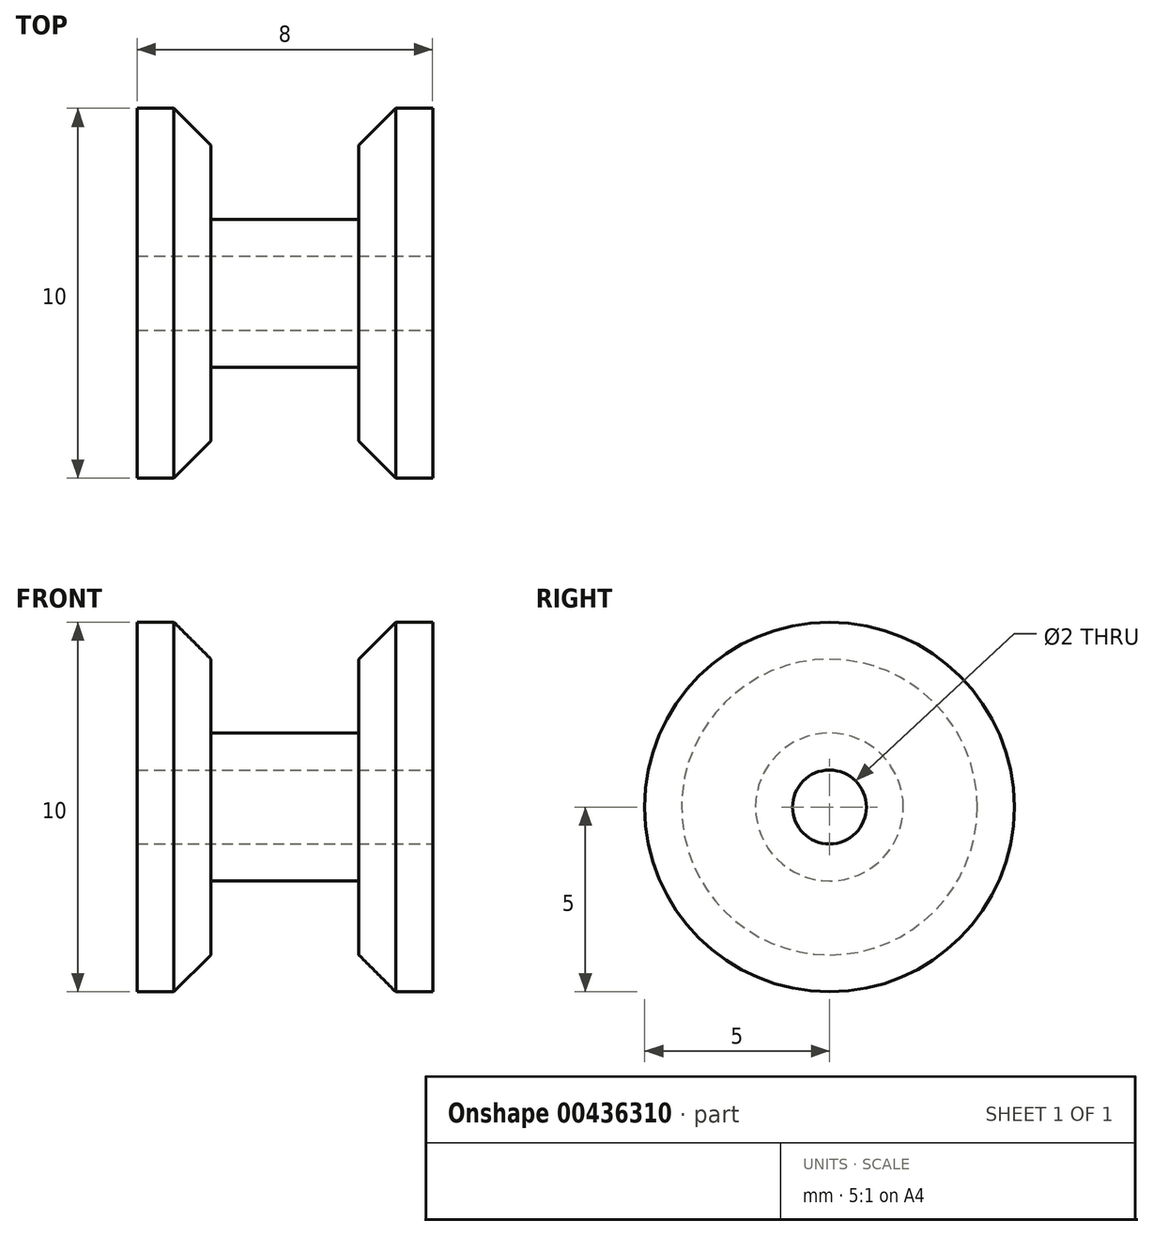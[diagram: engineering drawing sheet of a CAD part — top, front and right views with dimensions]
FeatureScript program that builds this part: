
annotation { "Feature Type Name" : "Feature", "Feature Type Description" : "" }
export const myFeature = defineFeature(function(context is Context, id is Id, definition is map)
    precondition{}
    {
        {
            var Q0;
            Q0=qCreatedBy(makeId("Top.planeOp"),FACE);
            var sketch = newSketch(context, id + "F0", { "sketchPlane" : qUnion([Q0])});
            skLineSegment(sketch, "E0", {"start": v(-2.83, 0) * mm, "end": v(-2.83, 5) * mm});
            skLineSegment(sketch, "E1", {"start": v(-2.83, 5) * mm, "end": v(-0.83, 5) * mm});
            skLineSegment(sketch, "E2", {"start": v(-0.83, 5) * mm, "end": v(-0.83, 2) * mm});
            skLineSegment(sketch, "E3", {"start": v(-0.83, 2) * mm, "end": v(3.17, 2) * mm});
            skLineSegment(sketch, "E4", {"start": v(3.17, 2) * mm, "end": v(3.17, 5) * mm});
            skLineSegment(sketch, "E5", {"start": v(3.17, 5) * mm, "end": v(5.17, 5) * mm});
            skLineSegment(sketch, "E6", {"start": v(5.17, 5) * mm, "end": v(5.17, 0) * mm});
            skLineSegment(sketch, "E7", {"start": v(5.17, 0) * mm, "end": v(-2.83, 0) * mm});
            skLineSegment(sketch, "E8", {"start": v(-2.83, 1) * mm, "end": v(5.17, 1) * mm});
            skSolve(sketch);
        }
        {
            var Q0;
            {var subQ0=sQuery(id+"F0.wireOp",EDGE,"E1");Q0=makeQuery(id+"F0.imprint","IMPRINT",FACE,{"disambiguationData":[TD([[makeQuery(id+"F0.imprint","IMPRINT",EDGE,{"derivedFrom":subQ0}),-1.0]])]});}
            var Q1;
            Q1=sQuery(id+"F0.wireOp",EDGE,"E7");
            revolve(context, id + "F1", {"entities" : qUnion([Q0]), "axis" : qUnion([Q1]), "revolveType" : RevolveType.FULL});
        }
        {
            var Q0;
            Q0=makeQuery(id+"F1.opRevolve","SWEPT_EDGE",EDGE,{"disambiguationData":[OSD([sQuery(id+"F0.wireOp",EDGE,"E1"),sQuery(id+"F0.wireOp",EDGE,"E2")])]});
            var Q1;
            Q1=makeQuery(id+"F1.opRevolve","SWEPT_EDGE",EDGE,{"disambiguationData":[OSD([sQuery(id+"F0.wireOp",EDGE,"E4"),sQuery(id+"F0.wireOp",EDGE,"E5")])]});
            chamfer(context, id + "F2", {"entities" : qUnion([Q0, Q1]), "width" : 1 * mm, "tangentPropagation" : true});
        }
    });
